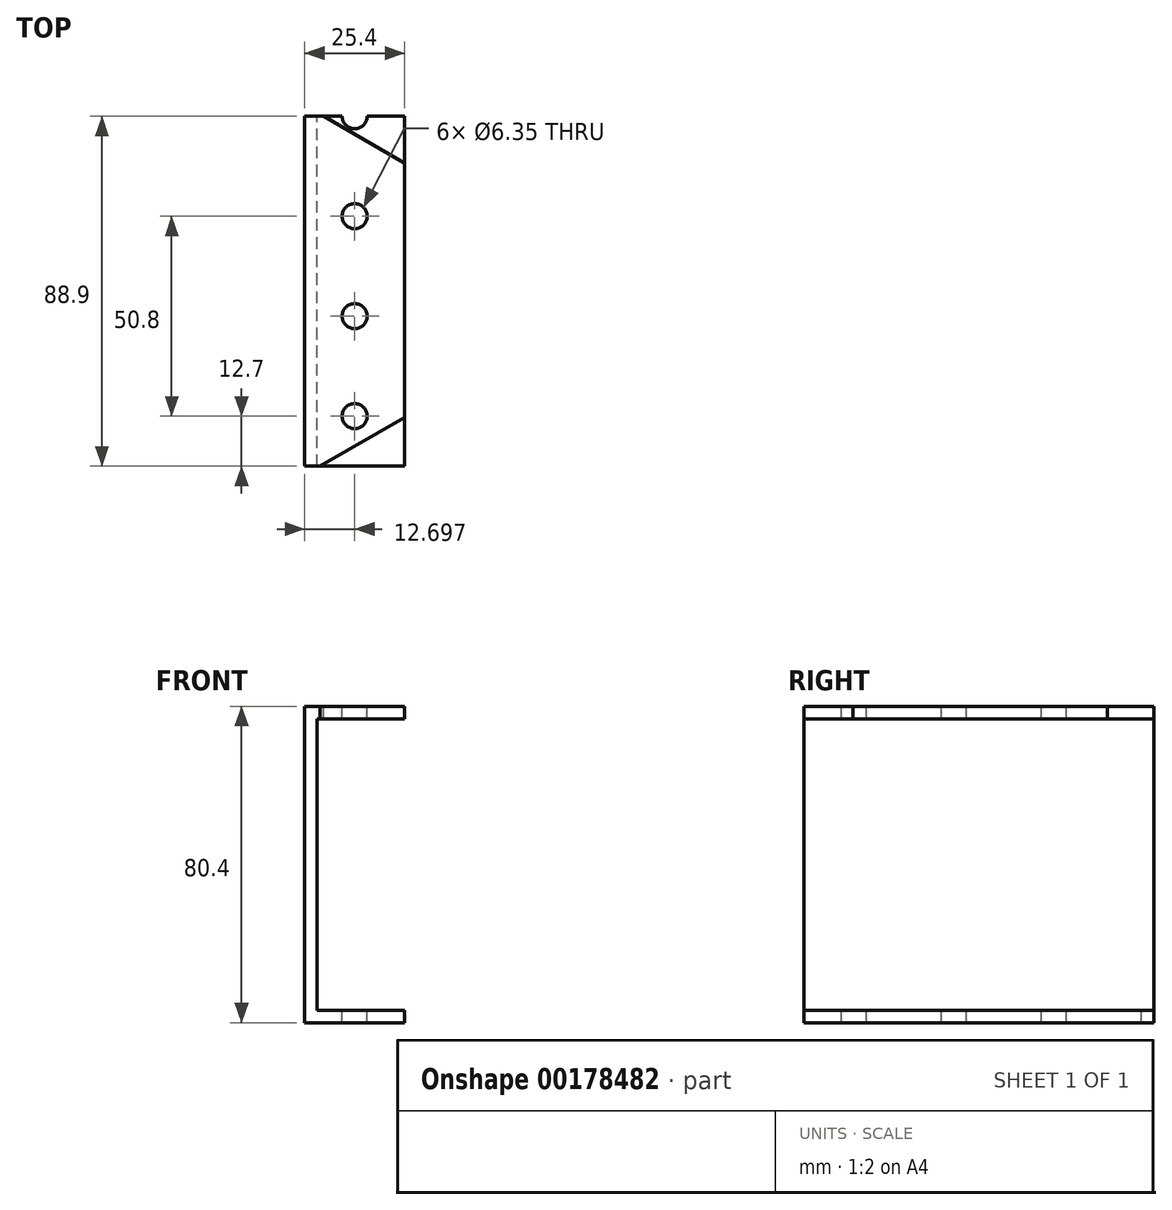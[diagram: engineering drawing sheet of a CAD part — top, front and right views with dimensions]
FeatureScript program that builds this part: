
annotation { "Feature Type Name" : "Feature", "Feature Type Description" : "" }
export const myFeature = defineFeature(function(context is Context, id is Id, definition is map)
    precondition{}
    {
        {
            var Q0;
            Q0=qCreatedBy(makeId("Front.planeOp"),FACE);
            var sketch = newSketch(context, id + "F0", { "sketchPlane" : qUnion([Q0])});
            skLineSegment(sketch, "E0", {"start": v(-21.92, 44.68) * mm, "end": v(-21.92, -35.72) * mm});
            skLineSegment(sketch, "E1", {"start": v(-21.92, 44.68) * mm, "end": v(3.48, 44.68) * mm});
            skLineSegment(sketch, "E2", {"start": v(-21.92, -35.72) * mm, "end": v(3.48, -35.72) * mm});
            skLineSegment(sketch, "E3", {"start": v(3.48, -35.72) * mm, "end": v(3.48, -32.54) * mm});
            skLineSegment(sketch, "E4", {"start": v(3.48, -32.54) * mm, "end": v(-18.75, -32.54) * mm});
            skLineSegment(sketch, "E5", {"start": v(-18.75, -32.54) * mm, "end": v(-18.75, 41.5) * mm});
            skLineSegment(sketch, "E6", {"start": v(-18.75, 41.5) * mm, "end": v(3.48, 41.5) * mm});
            skLineSegment(sketch, "E7", {"start": v(3.48, 41.5) * mm, "end": v(3.48, 44.68) * mm});
            skSolve(sketch);
        }
        {
            var Q0;
            Q0=makeQuery(id+"F0.imprint","IMPRINT",FACE,{"disambiguationData":[TD([[makeQuery(id+"F0.imprint","IMPRINT",EDGE,{"derivedFrom":sQuery(id+"F0.wireOp",EDGE,"E0")}),1.0]])]});
            extrude(context, id + "F1", {"entities" : qUnion([Q0]), "depth" : 88.9 * mm});
        }
        {
            var Q0;
            Q0=makeQuery(id+"F1.opExtrude","SWEPT_FACE",FACE,{"disambiguationData":[OSD([sQuery(id+"F0.wireOp",EDGE,"E1")])]});
            var sketch = newSketch(context, id + "F2", { "sketchPlane" : qUnion([Q0])});
            skCircle(sketch, "E8", {"center": v(-9.22, -76.2) * mm, "radius": 3.18 * mm});
            skCircle(sketch, "E9.0.1.0", {"center": v(-9.22, -50.8) * mm, "radius": 3.18 * mm});
            skCircle(sketch, "E9.0.2.0", {"center": v(-9.22, -25.4) * mm, "radius": 3.18 * mm});
            skCircle(sketch, "E9.0.3.0", {"center": v(-9.22, 0) * mm, "radius": 3.18 * mm});
            skCircle(sketch, "E9.1.0.0", {"center": v(-34.62, -76.2) * mm, "radius": 3.18 * mm});
            skCircle(sketch, "E9.1.1.0", {"center": v(-34.62, -50.8) * mm, "radius": 3.18 * mm});
            skCircle(sketch, "E9.1.2.0", {"center": v(-34.62, -25.4) * mm, "radius": 3.18 * mm});
            skCircle(sketch, "E9.1.3.0", {"center": v(-34.62, 0) * mm, "radius": 3.18 * mm});
            skLineSegment(sketch, "E9.direction1", {"start": v(-9.22, -76.2) * mm, "end": v(-34.62, -76.2) * mm, "construction": true});
            skLineSegment(sketch, "E9.direction2", {"start": v(-9.22, -76.2) * mm, "end": v(-9.22, -50.8) * mm, "construction": true});
            skSolve(sketch);
        }
        {
            var Q0;
            Q0 = qSketchRegion(id + "F2", true);
            extrude(context, id + "F3", {"entities" : qUnion([Q0]), "operationType" : NewBodyOperationType.REMOVE, "oppositeDirection" : true, "depth" : 101.6 * mm});
        }
        {
            var Q0;
            Q0=makeQuery(id+"F1.opExtrude","SWEPT_FACE",FACE,{"disambiguationData":[OSD([sQuery(id+"F0.wireOp",EDGE,"E1")])]});
            var sketch = newSketch(context, id + "F4", { "sketchPlane" : qUnion([Q0])});
            skLineSegment(sketch, "E10", {"start": v(-17.96, -88.9) * mm, "end": v(3.48, -76.52) * mm});
            skLineSegment(sketch, "E11", {"start": v(-17.16, 0) * mm, "end": v(3.48, -11.92) * mm});
            skSolve(sketch);
        }
        {
            var Q0;
            {var subQ10=sQuery(id+"F4.wireOp",EDGE,"E11");Q0=makeQuery(id+"F4.imprint","IMPRINT",FACE,{"disambiguationData":[TD([[makeQuery(id+"F4.imprint","IMPRINT",EDGE,{"derivedFrom":subQ10}),1.0]])]});}
            var Q1;
            {var subQ0=sQuery(id+"F4.wireOp",EDGE,"E10");Q1=makeQuery(id+"F4.imprint","IMPRINT",FACE,{"disambiguationData":[TD([[makeQuery(id+"F4.imprint","IMPRINT",EDGE,{"derivedFrom":subQ0}),-1.0]])]});}
            extrude(context, id + "F5", {"entities" : qUnion([Q0, Q1]), "operationType" : NewBodyOperationType.REMOVE, "oppositeDirection" : true, "depth" : 3.17 * mm});
        }
    });
